# Revit family: RAR1
name_source: partatom
category: Lighting Fixtures
units: mm (PartAtom-declared; Revit-internal decimal feet)

## family parameters
Always vertical = Yes
Cut with Voids When Loaded = No
Light Source = Yes
OmniClass Number = 23.80.70.14.21
OmniClass Title = Street and Roadway Lighting
Part Type = Normal
Room Calculation Point = No
Round Connector Dimension = Use Diameter
Shared = No
Work Plane-Based = No

## types (1)
- RAR1
    Apparent Load = 20 VA
    Assembly Code = D5020200
    Center Width = 3 "
    Certifications = UL,CSA,Wet Listed, Damp Listed, ANSI 3G Vibration Rated
    Color Filter = 16777215
    Color Temperature = 0 K
    Default Elevation = 0 "
    Depth = 18.44 "
    Description = With a new spin on a classic rectilinear form, Ratio brings the traditional shoebox aesthetic into the next generation of LED lighting. Ratio features a dense optical array which provides reduced pixilation and increased visual comfort without compromising performance. Designed for sustained, long-term performance with advanced thermal management, an elegantly simple heat sink, and industry leading surge protection.
    Dimming Lamp Color Temperature Shift = <None>
    Emit Shape Visible in Rendering = No
    Emit from Rectangle Length = 4.44 "
    Emit from Rectangle Width = 11 "
    Finish = Powder Coat-Black
    Fixture Height = 7.5 "
    Lamp = default
    Lens = Glass-Temper Molded
    Manufacturer = EXO
    Model = RAR1
    Number of Poles = 1
    Offset From Pole = 6.12 "
    Photometric Notes = More IES files download on Photometric Web Link
    Photometric Web File = RAR1-160L-100-3K7-2.ies
    Pole = Yes
    Pole Width = 4 "
    Power Factor = 1
    Series = Ratio
    Tilt Angle = 90.00°
    Type Comments = Lighting Fixture
    URL = https://www.currentlighting.com
    Voltage = 0 V
    Wattage Comments = 20W
    Width = 14 "

## geometry (parser evidence)
native form markers: Blend x2, Sweep x7
no freeform markers — native parametric forms only
